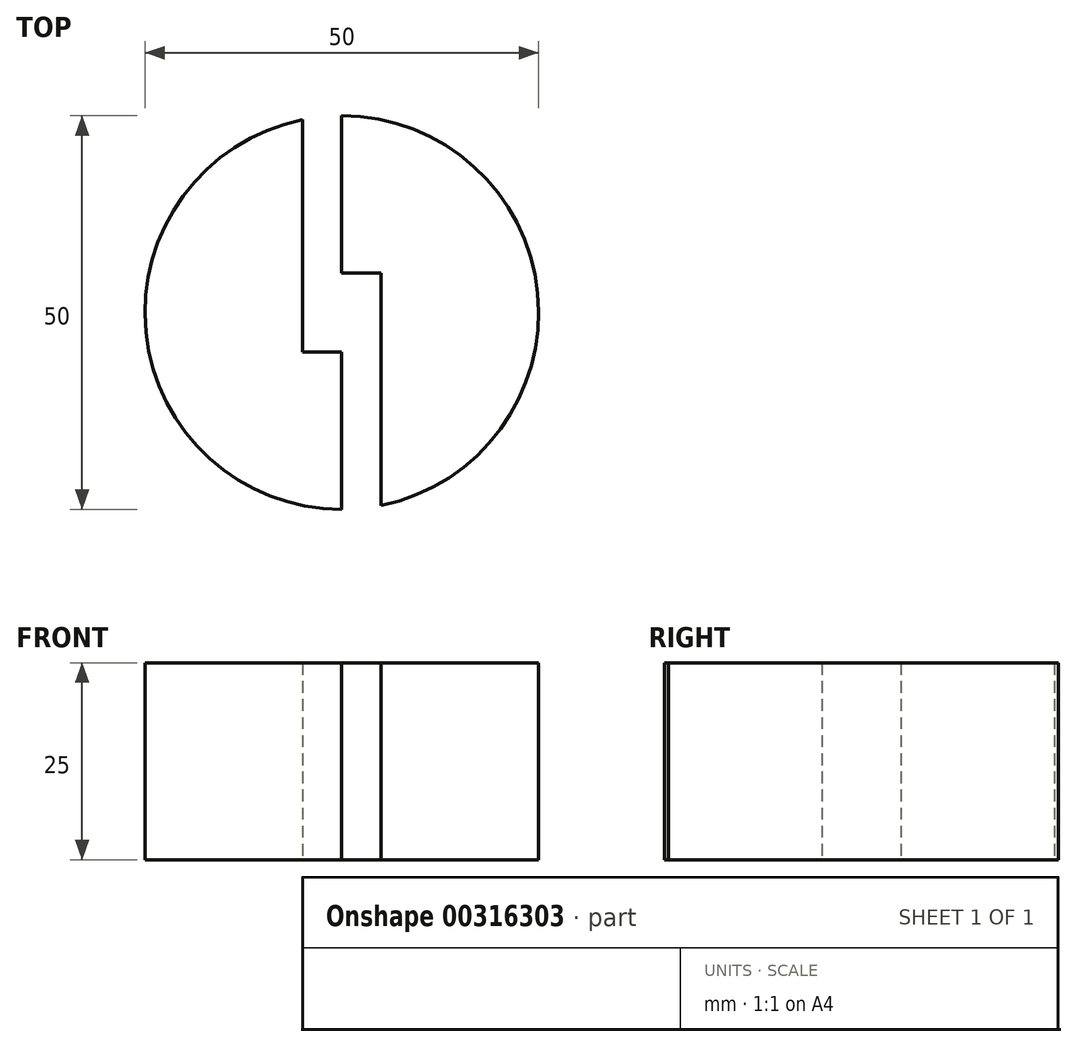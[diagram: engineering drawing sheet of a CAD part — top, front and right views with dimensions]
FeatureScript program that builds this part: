
annotation { "Feature Type Name" : "Feature", "Feature Type Description" : "" }
export const myFeature = defineFeature(function(context is Context, id is Id, definition is map)
    precondition{}
    {
        {
            var Q0;
            Q0=qCreatedBy(makeId("Top.planeOp"),FACE);
            var sketch = newSketch(context, id + "F0", { "sketchPlane" : qUnion([Q0])});
            skArc(sketch, "E0", {"start": v(-5, 24.5) * mm, "mid": v(-24.87, -2.51) * mm, "end": v(0, -25) * mm});
            skLineSegment(sketch, "E1.left", {"start": v(0, 5) * mm, "end": v(0, 25) * mm});
            skLineSegment(sketch, "E1.right", {"start": v(-5, 0) * mm, "end": v(-5, 24.5) * mm});
            skLineSegment(sketch, "E2.left", {"start": v(0, -5) * mm, "end": v(0, -25) * mm});
            skLineSegment(sketch, "E2.right", {"start": v(5, 0) * mm, "end": v(5, -24.5) * mm});
            skArc(sketch, "E3.trimOffspring", {"start": v(5, -24.5) * mm, "mid": v(24.87, 2.51) * mm, "end": v(0, 25) * mm});
            skLineSegment(sketch, "E4.bottom", {"start": v(0, 5) * mm, "end": v(5, 5) * mm});
            skLineSegment(sketch, "E4.top", {"start": v(-5, -5) * mm, "end": v(0, -5) * mm});
            skLineSegment(sketch, "E4.left", {"start": v(-5, 5) * mm, "end": v(-5, -5) * mm});
            skLineSegment(sketch, "E4.right", {"start": v(5, 5) * mm, "end": v(5, -5) * mm});
            skSolve(sketch);
        }
        {
            var Q0;
            Q0 = qSketchRegion(id + "F0", true);
            extrude(context, id + "F1", {"entities" : qUnion([Q0]), "depth" : 25 * mm});
        }
    });
